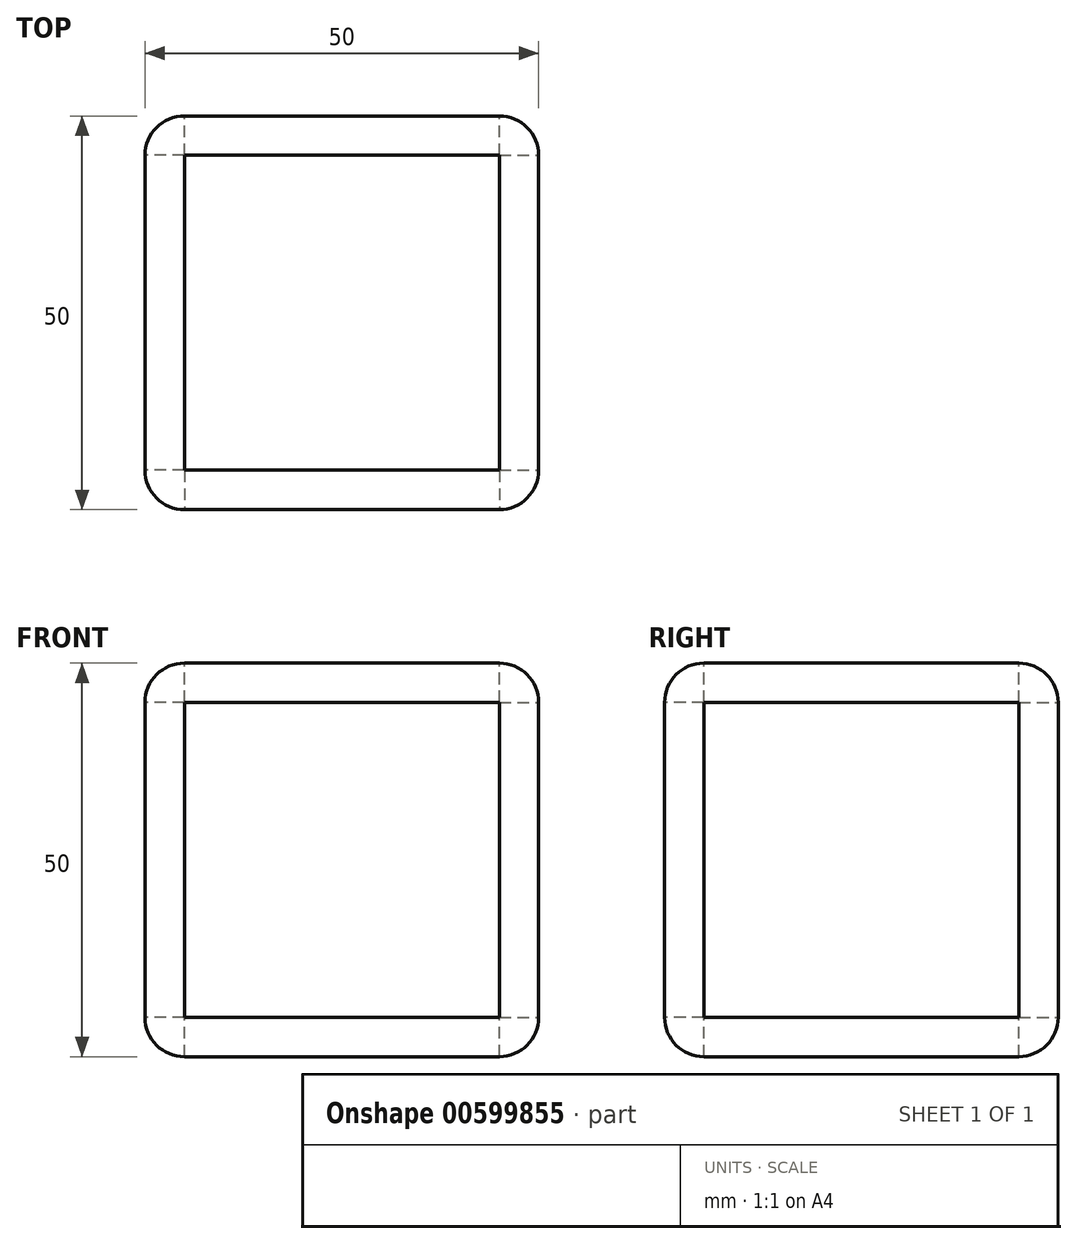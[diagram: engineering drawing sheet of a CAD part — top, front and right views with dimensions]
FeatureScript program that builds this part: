
annotation { "Feature Type Name" : "Feature", "Feature Type Description" : "" }
export const myFeature = defineFeature(function(context is Context, id is Id, definition is map)
    precondition{}
    {
        {
            var Q0;
            Q0=qCreatedBy(makeId("Front.planeOp"),FACE);
            var sketch = newSketch(context, id + "F0", { "sketchPlane" : qUnion([Q0])});
            skLineSegment(sketch, "E0.bottom", {"start": v(-26.12, 13.7) * mm, "end": v(23.88, 13.7) * mm});
            skLineSegment(sketch, "E0.top", {"start": v(-26.12, -36.3) * mm, "end": v(23.88, -36.3) * mm});
            skLineSegment(sketch, "E0.left", {"start": v(-26.12, 13.7) * mm, "end": v(-26.12, -36.3) * mm});
            skLineSegment(sketch, "E0.right", {"start": v(23.88, 13.7) * mm, "end": v(23.88, -36.3) * mm});
            skSolve(sketch);
        }
        {
            var Q0;
            Q0=makeQuery(id+"F0.imprint","IMPRINT",FACE,{"disambiguationData":[TD([[makeQuery(id+"F0.imprint","IMPRINT",EDGE,{"derivedFrom":sQuery(id+"F0.wireOp",EDGE,"E0.bottom")}),-1.0]])]});
            extrude(context, id + "F1", {"entities" : qUnion([Q0]), "depth" : 50 * mm, "offsetDistance" : 25 * mm});
        }
        {
            var Q0;
            Q0=makeQuery(id+"F1.opExtrude","CAP_FACE",FACE,{"disambiguationData":[OSD([sQuery(id+"F0.wireOp",EDGE,"E0.bottom"),sQuery(id+"F0.wireOp",EDGE,"E0.top"),sQuery(id+"F0.wireOp",EDGE,"E0.left"),sQuery(id+"F0.wireOp",EDGE,"E0.right")])],"isStart":false});
            fillet(context, id + "F2", {"entities" : qUnion([Q0]), "radius" : 5 * mm, "tangentPropagation" : true, "allowEdgeOverflow" : false});
        }
        {
            var Q0;
            Q0=makeQuery(id+"F1.opExtrude","SWEPT_FACE",FACE,{"disambiguationData":[OSD([sQuery(id+"F0.wireOp",EDGE,"E0.top")])]});
            fillet(context, id + "F3", {"entities" : qUnion([Q0]), "radius" : 5 * mm, "tangentPropagation" : true, "allowEdgeOverflow" : false});
        }
        {
            var Q0;
            Q0=makeQuery(id+"F1.opExtrude","CAP_FACE",FACE,{"disambiguationData":[OSD([sQuery(id+"F0.wireOp",EDGE,"E0.bottom"),sQuery(id+"F0.wireOp",EDGE,"E0.top"),sQuery(id+"F0.wireOp",EDGE,"E0.left"),sQuery(id+"F0.wireOp",EDGE,"E0.right")])],"isStart":true});
            fillet(context, id + "F4", {"entities" : qUnion([Q0]), "radius" : 5 * mm, "tangentPropagation" : true, "allowEdgeOverflow" : false});
        }
        {
            var Q0;
            Q0=makeQuery(id+"F1.opExtrude","SWEPT_FACE",FACE,{"disambiguationData":[OSD([sQuery(id+"F0.wireOp",EDGE,"E0.left")])]});
            fillet(context, id + "F5", {"entities" : qUnion([Q0]), "radius" : 5 * mm, "tangentPropagation" : true, "allowEdgeOverflow" : false});
        }
        {
            var Q0;
            Q0=makeQuery(id+"F1.opExtrude","SWEPT_FACE",FACE,{"disambiguationData":[OSD([sQuery(id+"F0.wireOp",EDGE,"E0.bottom")])]});
            fillet(context, id + "F6", {"entities" : qUnion([Q0]), "radius" : 5 * mm, "tangentPropagation" : true, "allowEdgeOverflow" : false});
        }
        {
            var Q0;
            Q0=makeQuery(id+"F1.opExtrude","SWEPT_FACE",FACE,{"disambiguationData":[OSD([sQuery(id+"F0.wireOp",EDGE,"E0.bottom")])]});
            extrude(context, id + "F7", {"entities" : qUnion([Q0]), "operationType" : NewBodyOperationType.REMOVE, "oppositeDirection" : true, "depth" : 80 * mm, "offsetDistance" : 25 * mm});
        }
        {
            var Q0;
            Q0=makeQuery(id+"F1.opExtrude","SWEPT_FACE",FACE,{"disambiguationData":[OSD([sQuery(id+"F0.wireOp",EDGE,"E0.right")])]});
            extrude(context, id + "F8", {"entities" : qUnion([Q0]), "operationType" : NewBodyOperationType.REMOVE, "oppositeDirection" : true, "depth" : 25 * mm, "offsetDistance" : 25 * mm});
        }
        {
            var Q0;
            Q0=makeQuery(id+"F1.opExtrude","SWEPT_FACE",FACE,{"disambiguationData":[OSD([sQuery(id+"F0.wireOp",EDGE,"E0.left")])]});
            extrude(context, id + "F9", {"entities" : qUnion([Q0]), "operationType" : NewBodyOperationType.REMOVE, "oppositeDirection" : true, "depth" : 25 * mm, "offsetDistance" : 25 * mm});
        }
        {
            var Q0;
            Q0=makeQuery(id+"F1.opExtrude","CAP_FACE",FACE,{"disambiguationData":[OSD([sQuery(id+"F0.wireOp",EDGE,"E0.bottom"),sQuery(id+"F0.wireOp",EDGE,"E0.top"),sQuery(id+"F0.wireOp",EDGE,"E0.left"),sQuery(id+"F0.wireOp",EDGE,"E0.right")])],"isStart":false});
            extrude(context, id + "F10", {"entities" : qUnion([Q0]), "operationType" : NewBodyOperationType.REMOVE, "oppositeDirection" : true, "depth" : 25 * mm, "offsetDistance" : 25 * mm});
        }
        {
            var Q0;
            Q0=makeQuery(id+"F1.opExtrude","CAP_FACE",FACE,{"disambiguationData":[OSD([sQuery(id+"F0.wireOp",EDGE,"E0.bottom"),sQuery(id+"F0.wireOp",EDGE,"E0.top"),sQuery(id+"F0.wireOp",EDGE,"E0.left"),sQuery(id+"F0.wireOp",EDGE,"E0.right")])],"isStart":true});
            extrude(context, id + "F11", {"entities" : qUnion([Q0]), "operationType" : NewBodyOperationType.REMOVE, "oppositeDirection" : true, "depth" : 25 * mm, "offsetDistance" : 25 * mm});
        }
    });
